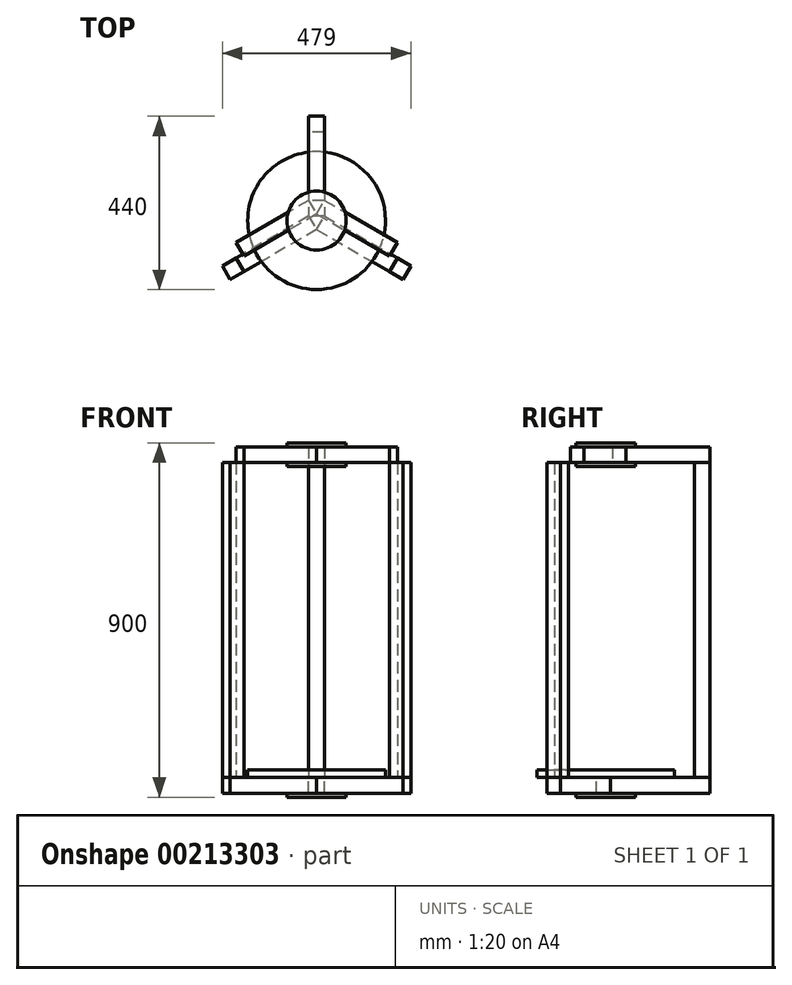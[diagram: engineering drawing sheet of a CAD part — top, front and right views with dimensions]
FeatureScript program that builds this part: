
annotation { "Feature Type Name" : "Feature", "Feature Type Description" : "" }
export const myFeature = defineFeature(function(context is Context, id is Id, definition is map)
    precondition{}
    {
        {
            var Q0;
            Q0=qCreatedBy(makeId("Top.planeOp"),FACE);
            var sketch = newSketch(context, id + "F0", { "sketchPlane" : qUnion([Q0])});
            skCircle(sketch, "E0", {"center": v(0, 0) * mm, "radius": 175 * mm});
            skLineSegment(sketch, "E1", {"start": v(0, 0) * mm, "end": v(0, 300) * mm});
            skLineSegment(sketch, "E2", {"start": v(0, 0) * mm, "end": v(259.8, -150) * mm});
            skLineSegment(sketch, "E3", {"start": v(0, 0) * mm, "end": v(-259.8, -150) * mm});
            skLineSegment(sketch, "E4.bottom", {"start": v(20, 225) * mm, "end": v(-20, 225) * mm});
            skLineSegment(sketch, "E4.top", {"start": v(20, 265) * mm, "end": v(-20, 265) * mm});
            skLineSegment(sketch, "E4.left", {"start": v(20, 225) * mm, "end": v(20, 265) * mm});
            skLineSegment(sketch, "E4.right", {"start": v(-20, 225) * mm, "end": v(-20, 265) * mm});
            skPoint(sketch, "E4.middle", {"position": v(0, 245) * mm});
            skLineSegment(sketch, "E5.bottom", {"start": v(239.5, -115.18) * mm, "end": v(204.86, -95.18) * mm});
            skLineSegment(sketch, "E5.top", {"start": v(219.5, -149.82) * mm, "end": v(184.86, -129.82) * mm});
            skLineSegment(sketch, "E5.left", {"start": v(239.5, -115.18) * mm, "end": v(219.5, -149.82) * mm});
            skLineSegment(sketch, "E5.right", {"start": v(204.86, -95.18) * mm, "end": v(184.86, -129.82) * mm});
            skPoint(sketch, "E5.middle", {"position": v(212.18, -122.5) * mm});
            skLineSegment(sketch, "E6.bottom", {"start": v(-239.5, -115.18) * mm, "end": v(-204.86, -95.18) * mm});
            skLineSegment(sketch, "E6.top", {"start": v(-219.5, -149.82) * mm, "end": v(-184.86, -129.82) * mm});
            skLineSegment(sketch, "E6.left", {"start": v(-239.5, -115.18) * mm, "end": v(-219.5, -149.82) * mm});
            skLineSegment(sketch, "E6.right", {"start": v(-204.86, -95.18) * mm, "end": v(-184.86, -129.82) * mm});
            skPoint(sketch, "E6.middle", {"position": v(-212.18, -122.5) * mm});
            skPoint(sketch, "E6.middle.positionSnap0", {"position": v(229.5, -132.5) * mm});
            skPoint(sketch, "E6.centerSnap0", {"position": v(229.5, -132.5) * mm});
            skSolve(sketch);
        }
        {
            var Q0;
            {var subQ5=sQuery(id+"F0.wireOp",EDGE,"E4.right");Q0=makeQuery(id+"F0.imprint","IMPRINT",FACE,{"disambiguationData":[TD([[makeQuery(id+"F0.imprint","IMPRINT",EDGE,{"derivedFrom":subQ5}),-1.0]])]});}
            var Q1;
            {var subQ5=sQuery(id+"F0.wireOp",EDGE,"E4.left");Q1=makeQuery(id+"F0.imprint","IMPRINT",FACE,{"disambiguationData":[TD([[makeQuery(id+"F0.imprint","IMPRINT",EDGE,{"derivedFrom":subQ5}),1.0]])]});}
            extrude(context, id + "F1", {"entities" : qUnion([Q0, Q1]), "depth" : 800 * mm});
        }
        {
            var Q0;
            {var subQ0=sQuery(id+"F0.wireOp",EDGE,"E3");var subQ1=sQuery(id+"F0.wireOp",EDGE,"E0");var subQ2=makeQuery(id+"F0.imprint","INTERSECT",VERTEX,{"derivedFrom":[subQ1,subQ0]});Q0=makeQuery(id+"F0.imprint","IMPRINT",FACE,{"disambiguationData":[TD([[makeQuery(id+"F0.imprint","IMPRINT",EDGE,{"disambiguationData":[TD([[subQ2,1.0]])],"derivedFrom":subQ1}),1.0]])]});}
            var Q1;
            {var subQ0=sQuery(id+"F0.wireOp",EDGE,"E1");var subQ1=sQuery(id+"F0.wireOp",EDGE,"E0");var subQ2=makeQuery(id+"F0.imprint","INTERSECT",VERTEX,{"derivedFrom":[subQ1,subQ0]});Q1=makeQuery(id+"F0.imprint","IMPRINT",FACE,{"disambiguationData":[TD([[makeQuery(id+"F0.imprint","IMPRINT",EDGE,{"disambiguationData":[TD([[subQ2,1.0]])],"derivedFrom":subQ1}),1.0]])]});}
            var Q2;
            {var subQ0=sQuery(id+"F0.wireOp",EDGE,"E3");var subQ1=sQuery(id+"F0.wireOp",EDGE,"E0");var subQ2=makeQuery(id+"F0.imprint","INTERSECT",VERTEX,{"derivedFrom":[subQ1,subQ0]});Q2=makeQuery(id+"F0.imprint","IMPRINT",FACE,{"disambiguationData":[TD([[makeQuery(id+"F0.imprint","IMPRINT",EDGE,{"disambiguationData":[TD([[subQ2,-1.0]])],"derivedFrom":subQ1}),1.0]])]});}
            extrude(context, id + "F2", {"entities" : qUnion([Q0, Q1, Q2]), "depth" : 20 * mm});
        }
        {
            var Q0;
            Q0=qCreatedBy(makeId("Top.planeOp"),FACE);
            var sketch = newSketch(context, id + "F3", { "sketchPlane" : qUnion([Q0])});
            skLineSegment(sketch, "E7.bottom", {"start": v(20, 265) * mm, "end": v(-20, 265) * mm});
            skLineSegment(sketch, "E7.top", {"start": v(20, 11.55) * mm, "end": v(-20, 11.55) * mm});
            skLineSegment(sketch, "E7.left", {"start": v(20, 265) * mm, "end": v(20, 11.55) * mm});
            skLineSegment(sketch, "E7.right", {"start": v(-20, 265) * mm, "end": v(-20, 11.55) * mm});
            skPoint(sketch, "E7.middle", {"position": v(0, 138.27) * mm});
            skLineSegment(sketch, "E8.bottom", {"start": v(-20, 11.55) * mm, "end": v(-239.5, -115.18) * mm});
            skLineSegment(sketch, "E8.top", {"start": v(0, -23.1) * mm, "end": v(-219.5, -149.82) * mm});
            skLineSegment(sketch, "E8.left", {"start": v(-20, 11.55) * mm, "end": v(0, -23.1) * mm});
            skLineSegment(sketch, "E8.right", {"start": v(-239.5, -115.18) * mm, "end": v(-219.5, -149.82) * mm});
            skPoint(sketch, "E8.middle", {"position": v(-119.75, -69.14) * mm});
            skLineSegment(sketch, "E9.bottom", {"start": v(0, -23.1) * mm, "end": v(219.5, -149.82) * mm});
            skLineSegment(sketch, "E9.top", {"start": v(20, 11.55) * mm, "end": v(239.5, -115.18) * mm});
            skLineSegment(sketch, "E9.left", {"start": v(0, -23.1) * mm, "end": v(20, 11.55) * mm});
            skLineSegment(sketch, "E9.right", {"start": v(219.5, -149.82) * mm, "end": v(239.5, -115.18) * mm});
            skSolve(sketch);
        }
        {
            var Q0;
            Q0=makeQuery(id+"F3.imprint","IMPRINT",FACE,{"disambiguationData":[TD([[makeQuery(id+"F3.imprint","IMPRINT",EDGE,{"derivedFrom":sQuery(id+"F3.wireOp",EDGE,"E7.bottom")}),1.0]])]});
            var Q1;
            Q1=makeQuery(id+"F3.imprint","IMPRINT",FACE,{"disambiguationData":[TD([[makeQuery(id+"F3.imprint","IMPRINT",EDGE,{"derivedFrom":sQuery(id+"F3.wireOp",EDGE,"E9.bottom")}),1.0]])]});
            var Q2;
            Q2=makeQuery(id+"F3.imprint","IMPRINT",FACE,{"disambiguationData":[TD([[makeQuery(id+"F3.imprint","IMPRINT",EDGE,{"derivedFrom":sQuery(id+"F3.wireOp",EDGE,"E8.bottom")}),1.0]])]});
            extrude(context, id + "F4", {"entities" : qUnion([Q0, Q1, Q2]), "oppositeDirection" : true, "depth" : 40 * mm});
        }
        {
            var Q0;
            {var subQ5=sQuery(id+"F0.wireOp",EDGE,"E6.bottom");Q0=makeQuery(id+"F0.imprint","IMPRINT",FACE,{"disambiguationData":[TD([[makeQuery(id+"F0.imprint","IMPRINT",EDGE,{"derivedFrom":subQ5}),-1.0]])]});}
            var Q1;
            {var subQ5=sQuery(id+"F0.wireOp",EDGE,"E6.top");Q1=makeQuery(id+"F0.imprint","IMPRINT",FACE,{"disambiguationData":[TD([[makeQuery(id+"F0.imprint","IMPRINT",EDGE,{"derivedFrom":subQ5}),1.0]])]});}
            var Q2;
            {var subQ5=sQuery(id+"F0.wireOp",EDGE,"E5.top");Q2=makeQuery(id+"F0.imprint","IMPRINT",FACE,{"disambiguationData":[TD([[makeQuery(id+"F0.imprint","IMPRINT",EDGE,{"derivedFrom":subQ5}),-1.0]])]});}
            var Q3;
            {var subQ5=sQuery(id+"F0.wireOp",EDGE,"E5.bottom");Q3=makeQuery(id+"F0.imprint","IMPRINT",FACE,{"disambiguationData":[TD([[makeQuery(id+"F0.imprint","IMPRINT",EDGE,{"derivedFrom":subQ5}),1.0]])]});}
            extrude(context, id + "F5", {"entities" : qUnion([Q0, Q1, Q2, Q3]), "depth" : 800 * mm});
        }
        {
            var Q0;
            Q0=makeQuery(id+"F5.opExtrude","CAP_FACE",FACE,{"disambiguationData":[OSD([sQuery(id+"F0.wireOp",EDGE,"E6.bottom"),sQuery(id+"F0.wireOp",EDGE,"E6.top"),sQuery(id+"F0.wireOp",EDGE,"E6.left"),sQuery(id+"F0.wireOp",EDGE,"E6.right")])],"isStart":false});
            cPlane(context, id + "F6", {"entities" : qUnion([Q0]), "cplaneType" : CPlaneType.OFFSET, "offset" : 0 * mm, "width" : 150 * mm, "height" : 150 * mm});
        }
        {
            var Q0;
            Q0=qCreatedBy(id+"F6.planeOp",FACE);
            var sketch = newSketch(context, id + "F7", { "sketchPlane" : qUnion([Q0])});
            skLineSegment(sketch, "E10.bottom", {"start": v(20, 265) * mm, "end": v(-20, 265) * mm});
            skLineSegment(sketch, "E10.top", {"start": v(20, 51.55) * mm, "end": v(-20, 51.55) * mm});
            skLineSegment(sketch, "E10.left", {"start": v(20, 265) * mm, "end": v(20, 51.55) * mm});
            skLineSegment(sketch, "E10.right", {"start": v(-20, 265) * mm, "end": v(-20, 51.55) * mm});
            skPoint(sketch, "E10.middle", {"position": v(0, 158.27) * mm});
            skLineSegment(sketch, "E11.bottom", {"start": v(-20, 51.55) * mm, "end": v(-204.86, -55.18) * mm});
            skLineSegment(sketch, "E11.top", {"start": v(0, 16.9) * mm, "end": v(-184.86, -89.82) * mm});
            skLineSegment(sketch, "E11.left", {"start": v(-20, 51.55) * mm, "end": v(0, 16.9) * mm});
            skLineSegment(sketch, "E11.right", {"start": v(-204.86, -55.18) * mm, "end": v(-184.86, -89.82) * mm});
            skPoint(sketch, "E11.middle", {"position": v(-102.43, -19.14) * mm});
            skLineSegment(sketch, "E12.bottom", {"start": v(0, 16.9) * mm, "end": v(184.86, -89.82) * mm});
            skLineSegment(sketch, "E12.top", {"start": v(20, 51.55) * mm, "end": v(204.86, -55.18) * mm});
            skLineSegment(sketch, "E12.left", {"start": v(0, 16.9) * mm, "end": v(20, 51.55) * mm});
            skLineSegment(sketch, "E12.right", {"start": v(184.86, -89.82) * mm, "end": v(204.86, -55.18) * mm});
            skSolve(sketch);
        }
        {
            var Q0;
            Q0=makeQuery(id+"F7.imprint","IMPRINT",FACE,{"disambiguationData":[TD([[makeQuery(id+"F7.imprint","IMPRINT",EDGE,{"derivedFrom":sQuery(id+"F7.wireOp",EDGE,"E11.bottom")}),1.0]])]});
            var Q1;
            Q1=makeQuery(id+"F7.imprint","IMPRINT",FACE,{"disambiguationData":[TD([[makeQuery(id+"F7.imprint","IMPRINT",EDGE,{"derivedFrom":sQuery(id+"F7.wireOp",EDGE,"E10.bottom")}),1.0]])]});
            var Q2;
            Q2=makeQuery(id+"F7.imprint","IMPRINT",FACE,{"disambiguationData":[TD([[makeQuery(id+"F7.imprint","IMPRINT",EDGE,{"derivedFrom":sQuery(id+"F7.wireOp",EDGE,"E12.bottom")}),1.0]])]});
            extrude(context, id + "F8", {"entities" : qUnion([Q0, Q1, Q2]), "depth" : 40 * mm});
        }
        {
            var Q0;
            Q0=makeQuery(id+"F8.opExtrude","CAP_FACE",FACE,{"disambiguationData":[OSD([sQuery(id+"F7.wireOp",EDGE,"E10.bottom"),sQuery(id+"F7.wireOp",EDGE,"E10.top"),sQuery(id+"F7.wireOp",EDGE,"E10.left"),sQuery(id+"F7.wireOp",EDGE,"E10.right")])],"isStart":false});
            cPlane(context, id + "F9", {"entities" : qUnion([Q0]), "cplaneType" : CPlaneType.OFFSET, "offset" : 0 * mm, "width" : 150 * mm, "height" : 150 * mm});
        }
        {
            var Q0;
            Q0=qCreatedBy(id+"F9.planeOp",FACE);
            var sketch = newSketch(context, id + "F10", { "sketchPlane" : qUnion([Q0])});
            skCircle(sketch, "E13", {"center": v(0, 0) * mm, "radius": 75 * mm});
            skSolve(sketch);
        }
        {
            var Q0;
            Q0=makeQuery(id+"F10.imprint","IMPRINT",FACE,{"disambiguationData":[TD([[makeQuery(id+"F10.imprint","IMPRINT",EDGE,{"derivedFrom":sQuery(id+"F10.wireOp",EDGE,"E13")}),1.0]])]});
            extrude(context, id + "F11", {"entities" : qUnion([Q0]), "depth" : 10 * mm});
        }
        {
            var Q0;
            Q0=qCreatedBy(id+"F6.planeOp",FACE);
            var sketch = newSketch(context, id + "F12", { "sketchPlane" : qUnion([Q0])});
            skCircle(sketch, "E14", {"center": v(0, 0) * mm, "radius": 75 * mm});
            skSolve(sketch);
        }
        {
            var Q0;
            Q0=makeQuery(id+"F12.imprint","IMPRINT",FACE,{"disambiguationData":[TD([[makeQuery(id+"F12.imprint","IMPRINT",EDGE,{"derivedFrom":sQuery(id+"F12.wireOp",EDGE,"E14")}),1.0]])]});
            extrude(context, id + "F13", {"entities" : qUnion([Q0]), "oppositeDirection" : true, "depth" : 10 * mm});
        }
        {
            var Q0;
            Q0=makeQuery(id+"F4.opExtrude","CAP_FACE",FACE,{"disambiguationData":[OSD([sQuery(id+"F3.wireOp",EDGE,"E9.bottom"),sQuery(id+"F3.wireOp",EDGE,"E9.top"),sQuery(id+"F3.wireOp",EDGE,"E9.left"),sQuery(id+"F3.wireOp",EDGE,"E9.right")])],"isStart":false});
            cPlane(context, id + "F14", {"entities" : qUnion([Q0]), "cplaneType" : CPlaneType.OFFSET, "offset" : 0 * mm, "width" : 150 * mm, "height" : 150 * mm});
        }
        {
            var Q0;
            Q0=qCreatedBy(id+"F14.planeOp",FACE);
            var sketch = newSketch(context, id + "F15", { "sketchPlane" : qUnion([Q0])});
            skCircle(sketch, "E15", {"center": v(0, 0) * mm, "radius": 75 * mm});
            skSolve(sketch);
        }
        {
            var Q0;
            Q0=makeQuery(id+"F15.imprint","IMPRINT",FACE,{"disambiguationData":[TD([[makeQuery(id+"F15.imprint","IMPRINT",EDGE,{"derivedFrom":sQuery(id+"F15.wireOp",EDGE,"E15")}),1.0]])]});
            extrude(context, id + "F16", {"entities" : qUnion([Q0]), "depth" : 10 * mm});
        }
    });
